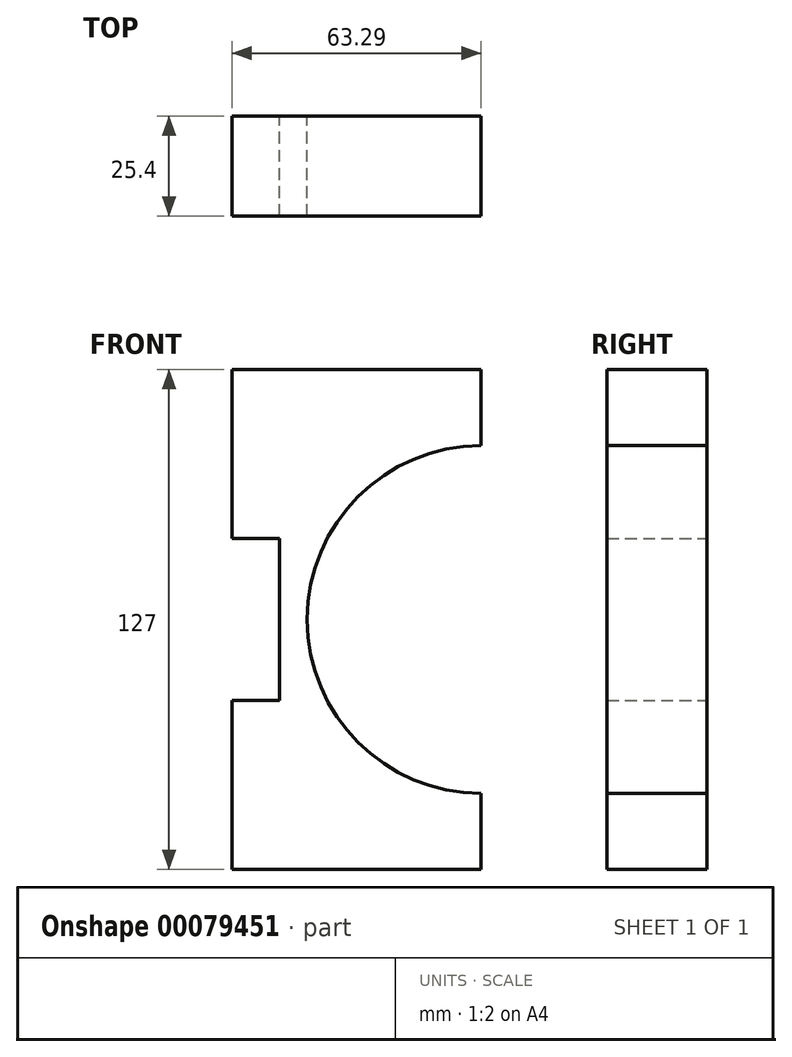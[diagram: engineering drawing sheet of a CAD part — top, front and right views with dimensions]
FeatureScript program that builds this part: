
annotation { "Feature Type Name" : "Feature", "Feature Type Description" : "" }
export const myFeature = defineFeature(function(context is Context, id is Id, definition is map)
    precondition{}
    {
        {
            var Q0;
            Q0=qCreatedBy(makeId("Front.planeOp"),FACE);
            var sketch = newSketch(context, id + "F0", { "sketchPlane" : qUnion([Q0])});
            skLineSegment(sketch, "E0.bottom", {"start": v(-56.7, 76.63) * mm, "end": v(6.59, 76.63) * mm});
            skLineSegment(sketch, "E0.top", {"start": v(-56.7, -50.37) * mm, "end": v(6.59, -50.37) * mm});
            skLineSegment(sketch, "E0.left", {"start": v(-56.7, 76.63) * mm, "end": v(-56.7, 33.66) * mm});
            skLineSegment(sketch, "E0.right", {"start": v(6.59, 76.63) * mm, "end": v(6.59, 57.3) * mm});
            skArc(sketch, "E1", {"start": v(6.59, 57.3) * mm, "mid": v(-37.6, 13.13) * mm, "end": v(6.59, -31.05) * mm});
            skPoint(sketch, "E2.start.orphan", {"position": v(-56.7, 13.13) * mm});
            skLineSegment(sketch, "E3.trimOffspring", {"start": v(6.59, -31.05) * mm, "end": v(6.59, -50.37) * mm});
            skLineSegment(sketch, "E4.bottom", {"start": v(-44.6, 33.66) * mm, "end": v(-56.7, 33.66) * mm});
            skLineSegment(sketch, "E4.top", {"start": v(-44.6, -7.4) * mm, "end": v(-56.7, -7.4) * mm});
            skLineSegment(sketch, "E4.left", {"start": v(-44.6, 33.66) * mm, "end": v(-44.6, -7.4) * mm});
            skPoint(sketch, "E4.right.start.orphan", {"position": v(-68.8, 33.66) * mm});
            skPoint(sketch, "E5.orphan", {"position": v(-68.8, -7.4) * mm});
            skLineSegment(sketch, "E6.trimOffspring", {"start": v(-56.7, -7.4) * mm, "end": v(-56.7, -50.37) * mm});
            skSolve(sketch);
        }
        {
            var Q0;
            Q0 = qSketchRegion(id + "F0", true);
            extrude(context, id + "F1", {"entities" : qUnion([Q0]), "depth" : 25.4 * mm});
        }
    });
